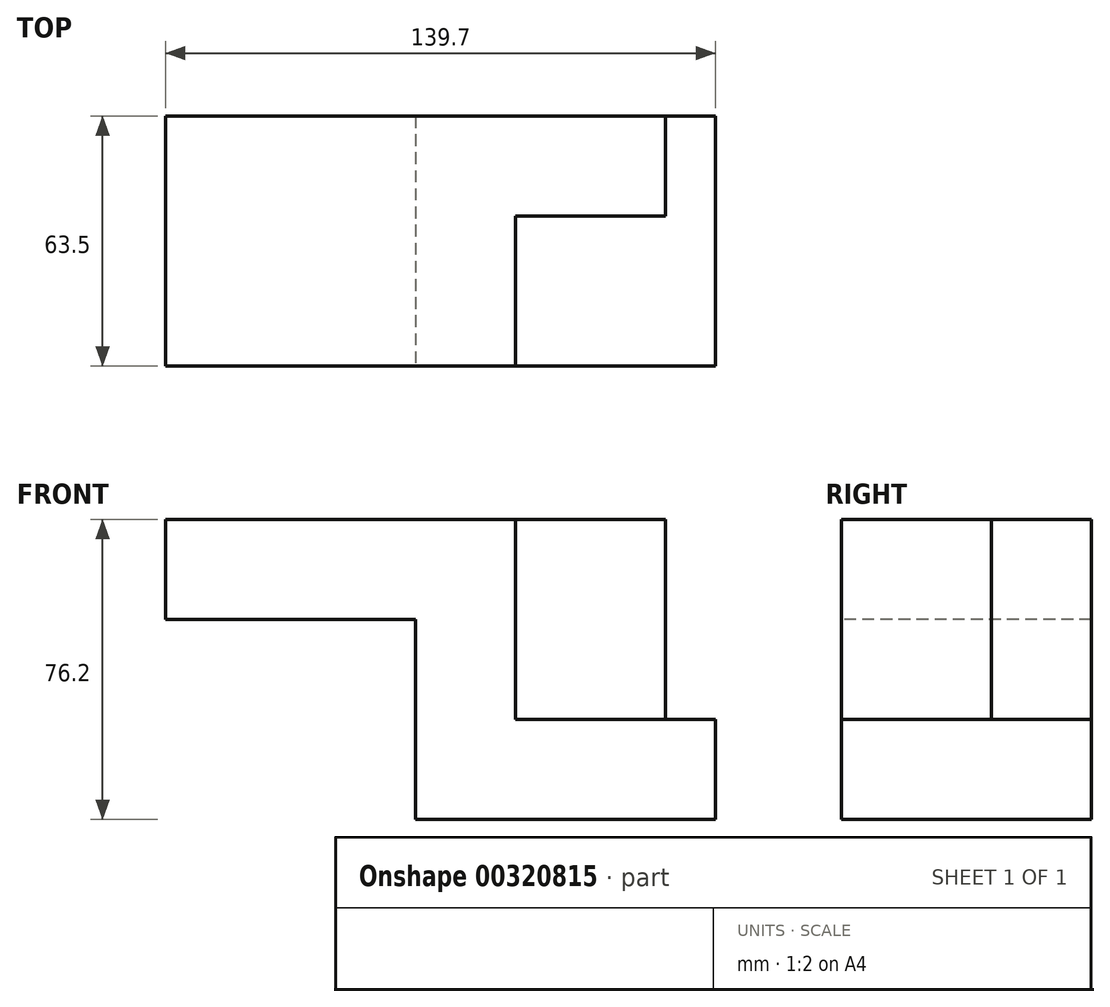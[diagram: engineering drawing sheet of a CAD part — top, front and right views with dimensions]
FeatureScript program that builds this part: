
annotation { "Feature Type Name" : "Feature", "Feature Type Description" : "" }
export const myFeature = defineFeature(function(context is Context, id is Id, definition is map)
    precondition{}
    {
        {
            var Q0;
            Q0=qCreatedBy(makeId("Top.planeOp"),FACE);
            var sketch = newSketch(context, id + "F0", { "sketchPlane" : qUnion([Q0])});
            skLineSegment(sketch, "E0", {"start": v(-35.8, 40.45) * mm, "end": v(40.4, 40.45) * mm});
            skLineSegment(sketch, "E1", {"start": v(40.4, 40.45) * mm, "end": v(40.4, -23.05) * mm});
            skLineSegment(sketch, "E2", {"start": v(40.4, -23.05) * mm, "end": v(-35.8, -23.05) * mm});
            skLineSegment(sketch, "E3", {"start": v(-35.8, -23.05) * mm, "end": v(-35.8, 40.45) * mm});
            skSolve(sketch);
        }
        {
            var Q0;
            Q0=makeQuery(id+"F0.imprint","IMPRINT",FACE,{"disambiguationData":[TD([[makeQuery(id+"F0.imprint","IMPRINT",EDGE,{"derivedFrom":sQuery(id+"F0.wireOp",EDGE,"E0")}),-1.0]])]});
            extrude(context, id + "F1", {"entities" : qUnion([Q0]), "depth" : 25.4 * mm});
        }
        {
            var Q0;
            Q0=makeQuery(id+"F1.opExtrude","CAP_FACE",FACE,{"disambiguationData":[OSD([sQuery(id+"F0.wireOp",EDGE,"E0"),sQuery(id+"F0.wireOp",EDGE,"E1"),sQuery(id+"F0.wireOp",EDGE,"E2"),sQuery(id+"F0.wireOp",EDGE,"E3")])],"isStart":false});
            var sketch = newSketch(context, id + "F2", { "sketchPlane" : qUnion([Q0])});
            skLineSegment(sketch, "E4", {"start": v(-35.8, -23.05) * mm, "end": v(-10.4, -23.05) * mm});
            skLineSegment(sketch, "E5", {"start": v(-10.4, -23.05) * mm, "end": v(-10.4, 15.05) * mm});
            skLineSegment(sketch, "E6", {"start": v(-10.4, 15.05) * mm, "end": v(27.7, 15.05) * mm});
            skLineSegment(sketch, "E7", {"start": v(27.7, 15.05) * mm, "end": v(27.7, 40.45) * mm});
            skLineSegment(sketch, "E8", {"start": v(27.7, 40.45) * mm, "end": v(-35.8, 40.45) * mm});
            skLineSegment(sketch, "E9", {"start": v(-35.8, 40.45) * mm, "end": v(-35.8, -23.05) * mm});
            skSolve(sketch);
        }
        {
            var Q0;
            Q0 = qSketchRegion(id + "F2", true);
            extrude(context, id + "F3", {"entities" : qUnion([Q0]), "operationType" : NewBodyOperationType.ADD, "depth" : 50.8 * mm});
        }
        {
            var Q0;
            Q0=makeQuery(id+"F3.boolean.opBoolean","MERGE",FACE,{"derivedFrom":[makeQuery(id+"F1.opExtrude","SWEPT_FACE",FACE,{"disambiguationData":[OSD([sQuery(id+"F0.wireOp",EDGE,"E3")])]}),makeQuery(id+"F3.opExtrude","SWEPT_FACE",FACE,{"disambiguationData":[OSD([sQuery(id+"F2.wireOp",EDGE,"E9")])]})]});
            var sketch = newSketch(context, id + "F4", { "sketchPlane" : qUnion([Q0])});
            skLineSegment(sketch, "E10", {"start": v(-40.45, 76.2) * mm, "end": v(-40.45, 50.8) * mm});
            skLineSegment(sketch, "E11", {"start": v(-40.45, 50.8) * mm, "end": v(23.05, 50.8) * mm});
            skLineSegment(sketch, "E12", {"start": v(23.05, 50.8) * mm, "end": v(23.05, 76.2) * mm});
            skLineSegment(sketch, "E13", {"start": v(23.05, 76.2) * mm, "end": v(-40.45, 76.2) * mm});
            skSolve(sketch);
        }
        {
            var Q0;
            Q0=makeQuery(id+"F4.imprint","IMPRINT",FACE,{"disambiguationData":[TD([[makeQuery(id+"F4.imprint","IMPRINT",EDGE,{"derivedFrom":sQuery(id+"F4.wireOp",EDGE,"E10")}),1.0]])]});
            extrude(context, id + "F5", {"entities" : qUnion([Q0]), "operationType" : NewBodyOperationType.ADD, "depth" : 63.5 * mm});
        }
    });
